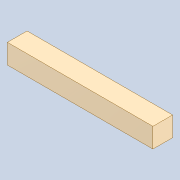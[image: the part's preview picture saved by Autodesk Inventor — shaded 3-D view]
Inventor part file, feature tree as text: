
AUTODESK INVENTOR PART (.ipt)
format: ipt  version: 2021 (Build 250183000, 183)  size: 75,264 bytes
history: native  units: in
note: dims shown in document units (in); Inventor stores cm internally (conversion verified against a paired STEP export)
features: extrude x1, sketch x1
ambient origin geometry x8: Origin, YZ Plane, XZ Plane, XY Plane, X Axis, Y Axis, Z Axis, Center Point
bodies: Solid1 (feature_tree)
feature tree (2):
  extrude  "Extrusion1"  Depth=2.3125in TaperAngle=0.0deg
  sketch  "Sketch1"  dims[d0=0.3125in d1=2.3125in d2=0.0in]
